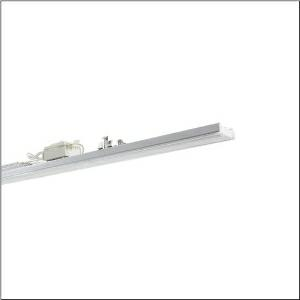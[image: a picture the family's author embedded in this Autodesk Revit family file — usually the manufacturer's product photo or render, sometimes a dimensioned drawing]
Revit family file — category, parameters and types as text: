
# Revit family: licross_11_recessed_ho_51te12dv4m2m3c
name_source: partatom
category: Lighting Fixtures
units: mm (PartAtom-declared; Revit-internal decimal feet)

## family parameters
Cut with Voids When Loaded = No
Host = Face
Light Source = No
Part Type = Normal
Room Calculation Point = No
Round Connector Dimension = Use Diameter
Shared = No

## types (1)
- --- (1 x LED, 1010 lm, 5.9 W, 4000K)
    Apparent Load = 6 VA
    CIE Flux Codes = 66 91 98 100 100
    Color Rendering = 80
    Color Temperature = 4000K
    Default Elevation = 1800 mm
    Description = Licross 11 Recessed HO, luminaire insert, of sheet steel, galvanised, coil coated, white, length: 2.250mm, width: 66mm, height: 67mm, LED rated luminous flux: 27.150lm, light colour: 840, SDCM (Standard Deviation of Colour Matching)MacAdam ≤ 2 SDCM (initial), control gear: DALI 2 (for two DALI lines), with plug, 6-pole, with phase selection, for trunking rail, 14-core, mains connection: 220..240V, AC, 50/60Hz, rated input power: 154W, for trunking rail, 14-core, internal wiring halogen-free, for emergency light function, converter,control gear: single battery element, battery: LiFePO4, 9Ah, primary optical cover: cover, of PMMA, light emission: direct distribution, primary light characteristic: symmetric, protection rating (complete): IP54, insulation class (complete): insulation class I (protective earthing), certification: CE, UKCA, protection symbol: D if used in an environment with non-conductive dust loads with corresponding accessories, impact resistance: IK06, permissible ambient temperature for indoor applications: +5..+35°C, standard: EN 60598-2-22, LABS conformity tested according to VDMA 24364:2018-05, reducing of maximum allowable ambient temperature of 5°C with ceiling mounting, corresponds to IFS (International Featured Standards) requirements for safety and quality in the food industry, The light source and the operating device comply with the requirements of the Ecodesign Regulation (EU) 2019/2020 and are replaceable in accordance with this regulation, packaging unit: 1 piece
    Height = 58 mm
    Lamp = 1 x LED
    Lamp Light Flux = 1010 lm
    Lamp Power = 5.9 W
    Lamp count = 1
    Length = 2250 mm
    Luminous efficacy = 171 lm/W
    Manufacturer = Siteco
    ModVariant = No
    Model = 51TE12DV4M2M3C
    Mounting Place = Ceiling
    Mounting Type = Pendant
    Number of Poles = 1
    OnlyDefault = Yes
    Power Factor = 1
    Product Name = Licross 11 Recessed HO
    Product group = luminaire insert | ceiling pendant
    ProductGroupID = 901
    Protection Class = Protection class I
    Protection Degree = IP 54
    RLX_Detail_Level = 1
    RLX_Emergency_Light_Flux = 0 lm
    RLX_Emergency_Type = 0
    RLX_Emergency_Type_DB = No
    RlxData = <blob elided: 30285 chars, md5=33a2a278>
    Socket = socket
    Standby Power = 0 W
    System Light Flux = 1010 lm
    System Power = 6 W
    Type Comments = : emergency light operation: 3 h
    Type Image = l_1296930.jpg
    URL = http://relux.com
    VarID = @adj_089619
    Voltage = 0 V
    Weight = 0.00 kg
    Width = 66 mm

## geometry (parser evidence)
native form markers: Blend x4, Sweep x10
no freeform markers — native parametric forms only
